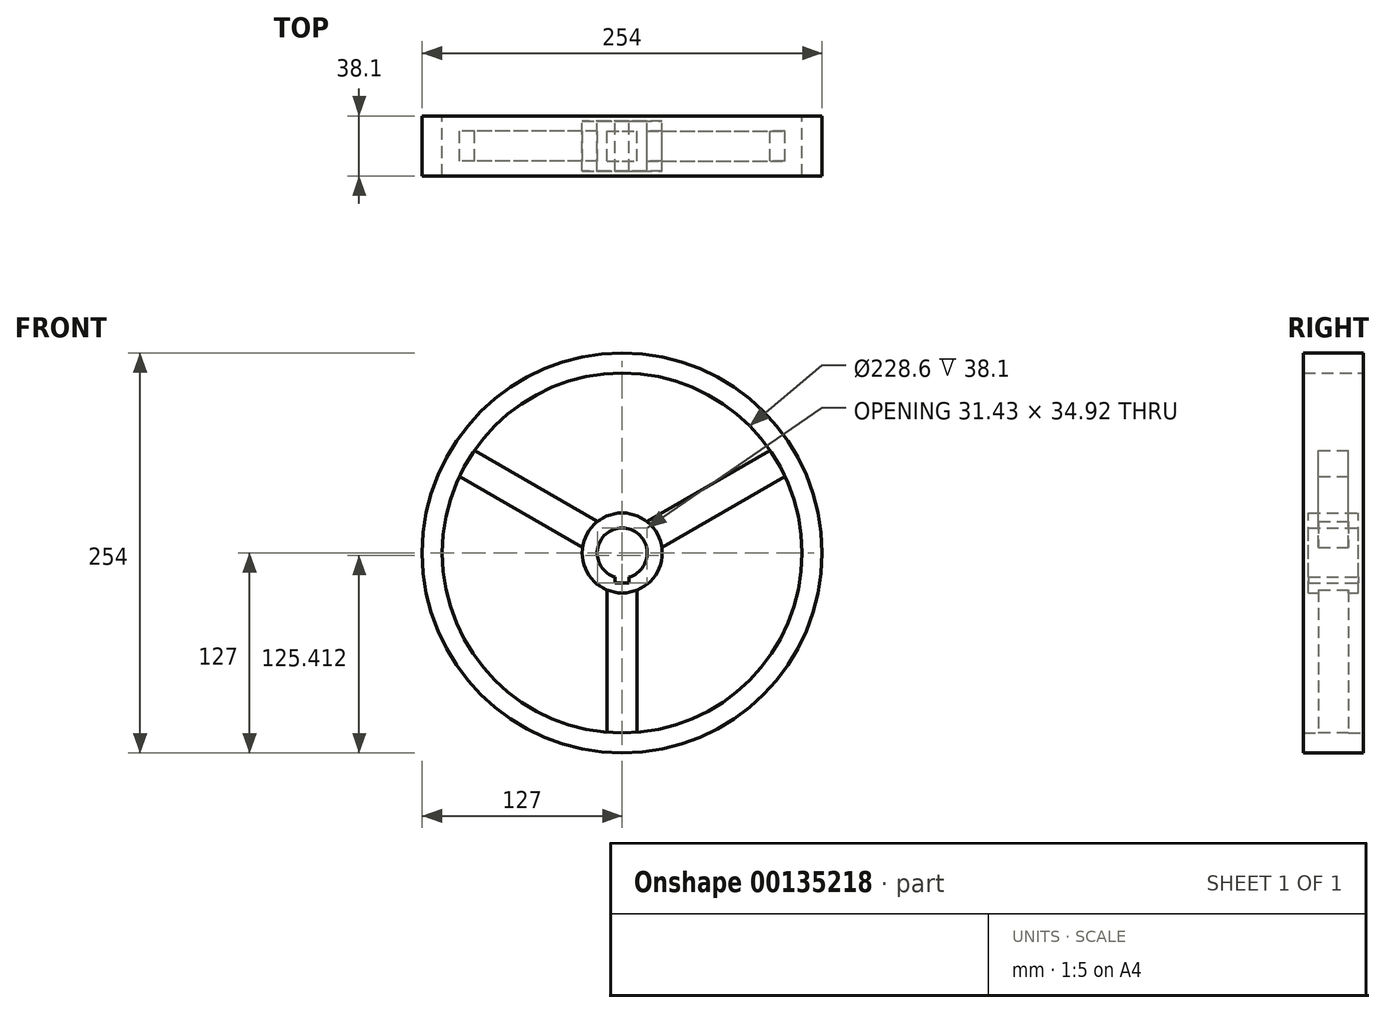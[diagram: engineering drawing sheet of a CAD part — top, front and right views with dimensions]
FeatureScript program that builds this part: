
annotation { "Feature Type Name" : "Feature", "Feature Type Description" : "" }
export const myFeature = defineFeature(function(context is Context, id is Id, definition is map)
    precondition{}
    {
        {
            var Q0;
            Q0=qCreatedBy(makeId("Front.planeOp"),FACE);
            var sketch = newSketch(context, id + "F0", { "sketchPlane" : qUnion([Q0])});
            skCircle(sketch, "E0", {"center": v(0, 0) * mm, "radius": 114.3 * mm});
            skCircle(sketch, "E1", {"center": v(0, 0) * mm, "radius": 127 * mm});
            skCircle(sketch, "E2", {"center": v(0, 0) * mm, "radius": 25.4 * mm});
            skArc(sketch, "E3", {"start": v(4.45, -15.24) * mm, "mid": v(0, 15.88) * mm, "end": v(-4.45, -15.24) * mm});
            skLineSegment(sketch, "E4.top", {"start": v(-4.45, -19.05) * mm, "end": v(4.45, -19.05) * mm});
            skLineSegment(sketch, "E4.left", {"start": v(-4.45, -15.24) * mm, "end": v(-4.45, -19.05) * mm});
            skLineSegment(sketch, "E5.MirrorCS", {"start": v(4.45, -15.24) * mm, "end": v(4.45, -19.05) * mm});
            skLineSegment(sketch, "E6", {"start": v(-9.53, -23.55) * mm, "end": v(-9.52, -113.9) * mm});
            skLineSegment(sketch, "E7", {"start": v(9.53, -23.55) * mm, "end": v(9.53, -113.9) * mm});
            skLineSegment(sketch, "E8", {"start": v(0, 0) * mm, "end": v(0, -76.04) * mm, "construction": true});
            skLineSegment(sketch, "E9.1.0", {"start": v(15.63, 20.02) * mm, "end": v(93.88, 65.2) * mm});
            skLineSegment(sketch, "E9.1.1", {"start": v(25.15, 3.52) * mm, "end": v(103.4, 48.7) * mm});
            skLineSegment(sketch, "E9.2.0", {"start": v(-25.15, 3.52) * mm, "end": v(-103.4, 48.7) * mm});
            skLineSegment(sketch, "E9.2.1", {"start": v(-15.63, 20.02) * mm, "end": v(-93.88, 65.2) * mm});
            skSolve(sketch);
        }
        {
            var Q0;
            Q0=makeQuery(id+"F0.imprint","IMPRINT",FACE,{"disambiguationData":[TD([[makeQuery(id+"F0.imprint","IMPRINT",EDGE,{"derivedFrom":sQuery(id+"F0.wireOp",EDGE,"E1")}),1.0]])]});
            var Q1;
            Q1=qCreatedBy(makeId("Front.planeOp"),FACE);
            extrude(context, id + "F1", {"entities" : qUnion([Q0]), "endBound" : BoundingType.SYMMETRIC, "endBoundEntityFace" : qUnion([Q1]), "depth" : 38.1 * mm});
        }
        {
            var Q0;
            Q0=makeQuery(id+"F0.imprint","IMPRINT",FACE,{"disambiguationData":[TD([[makeQuery(id+"F0.imprint","IMPRINT",EDGE,{"derivedFrom":sQuery(id+"F0.wireOp",EDGE,"E3")}),-1.0]])]});
            extrude(context, id + "F2", {"entities" : qUnion([Q0]), "endBound" : BoundingType.SYMMETRIC, "depth" : 31.75 * mm});
        }
        {
            var Q0;
            {var subQ0=sQuery(id+"F0.wireOp",EDGE,"E9.2.0");Q0=makeQuery(id+"F0.imprint","IMPRINT",FACE,{"disambiguationData":[TD([[makeQuery(id+"F0.imprint","IMPRINT",EDGE,{"derivedFrom":subQ0}),-1.0]])]});}
            var Q1;
            {var subQ0=sQuery(id+"F0.wireOp",EDGE,"E6");Q1=makeQuery(id+"F0.imprint","IMPRINT",FACE,{"disambiguationData":[TD([[makeQuery(id+"F0.imprint","IMPRINT",EDGE,{"derivedFrom":subQ0}),1.0]])]});}
            var Q2;
            {var subQ0=sQuery(id+"F0.wireOp",EDGE,"E9.1.0");Q2=makeQuery(id+"F0.imprint","IMPRINT",FACE,{"disambiguationData":[TD([[makeQuery(id+"F0.imprint","IMPRINT",EDGE,{"derivedFrom":subQ0}),-1.0]])]});}
            extrude(context, id + "F3", {"entities" : qUnion([Q0, Q1, Q2]), "operationType" : NewBodyOperationType.ADD, "endBound" : BoundingType.SYMMETRIC, "depth" : 19.05 * mm});
        }
    });
